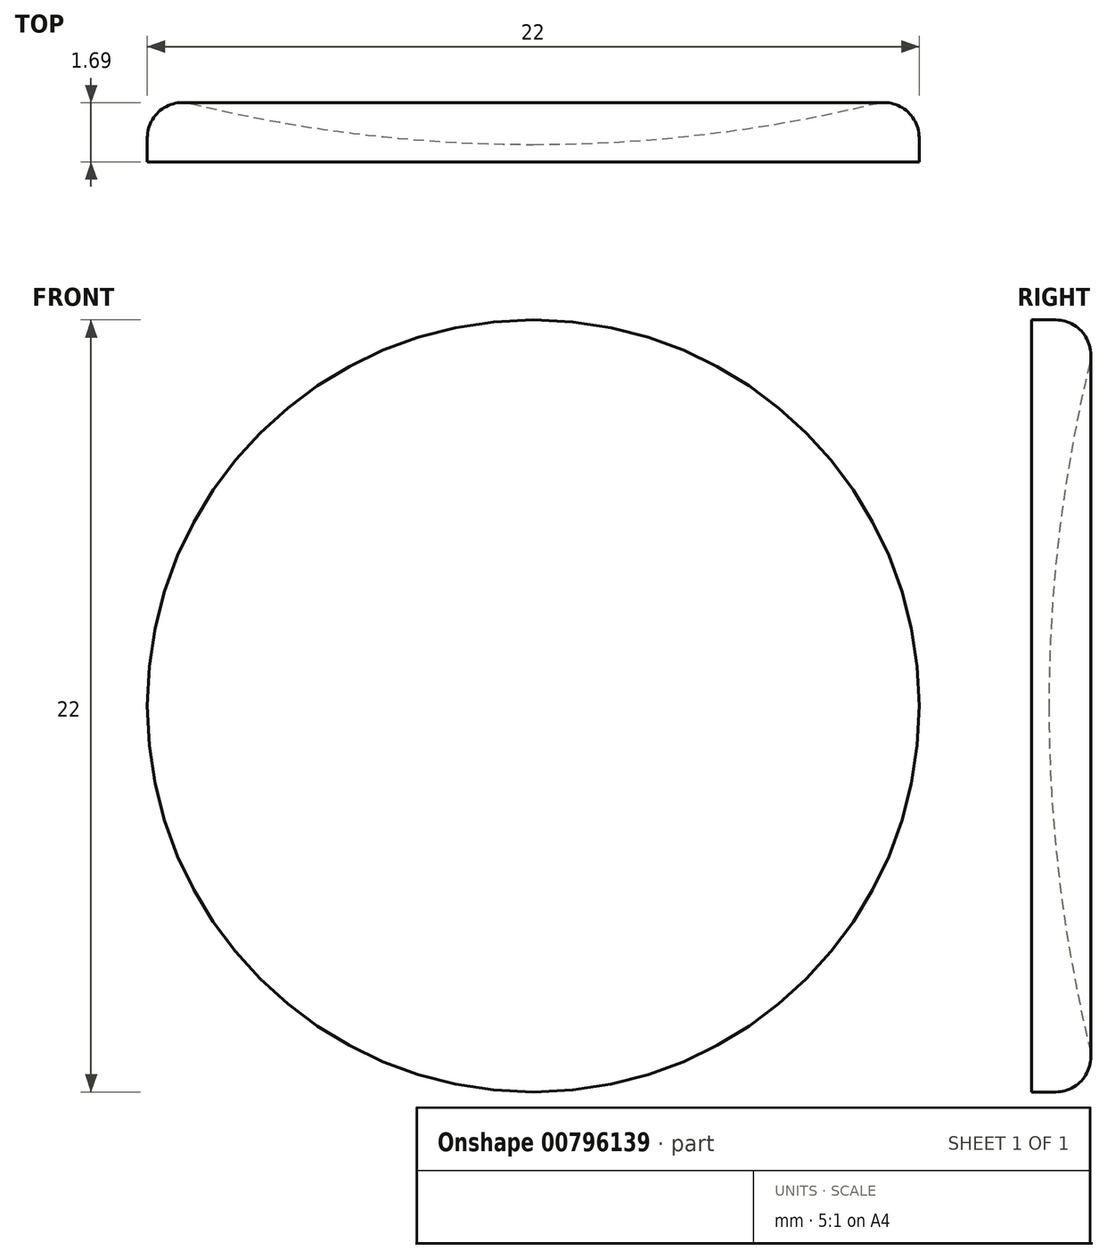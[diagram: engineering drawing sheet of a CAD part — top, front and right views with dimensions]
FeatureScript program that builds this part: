
annotation { "Feature Type Name" : "Feature", "Feature Type Description" : "" }
export const myFeature = defineFeature(function(context is Context, id is Id, definition is map)
    precondition{}
    {
        {
            var Q0;
            Q0=qCreatedBy(makeId("Top.planeOp"),FACE);
            var sketch = newSketch(context, id + "F0", { "sketchPlane" : qUnion([Q0])});
            skLineSegment(sketch, "E0", {"start": v(0, 42.01) * mm, "end": v(0, -30.07) * mm, "construction": true});
            skLineSegment(sketch, "E1", {"start": v(0, 0) * mm, "end": v(-11, 0) * mm});
            skLineSegment(sketch, "E2", {"start": v(-11, 0) * mm, "end": v(-11, 1.98) * mm});
            skArc(sketch, "E3", {"start": v(-11, 1.98) * mm, "mid": v(-5.55, 0.87) * mm, "end": v(0, 0.5) * mm});
            skSolve(sketch);
        }
        {
            var Q0;
            Q0=sQuery(id+"F0.wireOp",EDGE,"E3");
            var Q1;
            Q1=sQuery(id+"F0.wireOp",EDGE,"E1");
            var Q2;
            Q2=sQuery(id+"F0.wireOp",EDGE,"E2");
            var Q3;
            Q3=sQuery(id+"F0.wireOp",EDGE,"E0");
            revolve(context, id + "F1", {"bodyType" : ToolBodyType.SURFACE, "surfaceOperationType" : NewSurfaceOperationType.NEW, "surfaceEntities" : qUnion([Q0, Q1, Q2]), "axis" : qUnion([Q3]), "revolveType" : RevolveType.FULL});
        }
        {
            var Q0;
            Q0=makeQuery(id+"F1.opRevolve","SWEPT_EDGE",EDGE,{"disambiguationData":[OSD([sQuery(id+"F0.wireOp",VERTEX,"E2.end")])]});
            fillet(context, id + "F2", {"entities" : qUnion([Q0]), "radius" : 1 * mm, "tangentPropagation" : true, "allowEdgeOverflow" : false});
        }
    });
